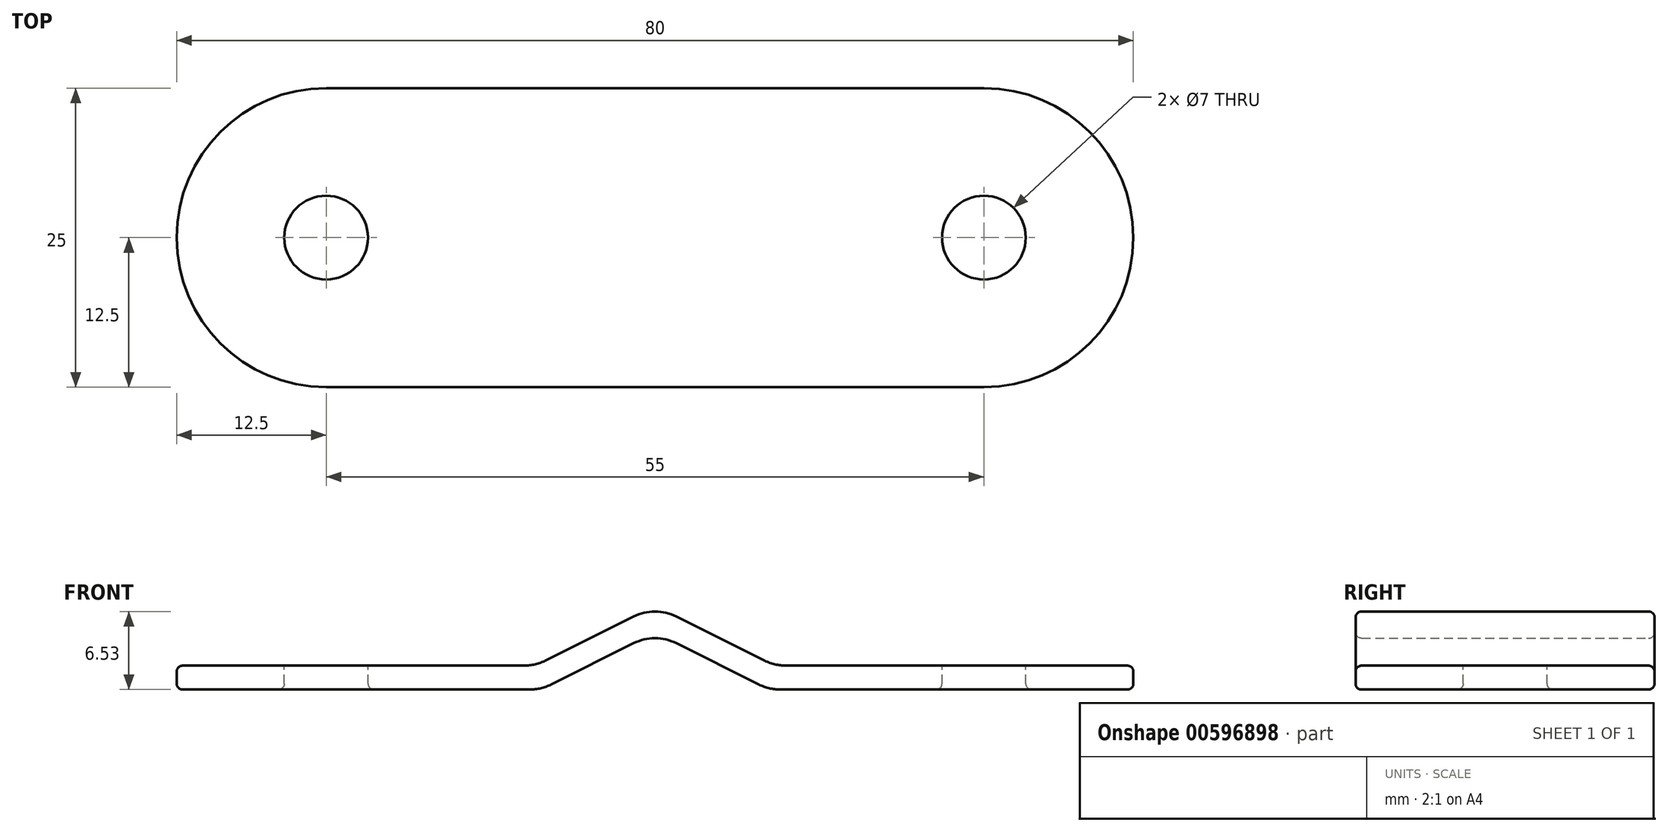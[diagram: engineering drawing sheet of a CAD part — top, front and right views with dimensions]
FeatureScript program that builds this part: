
annotation { "Feature Type Name" : "Feature", "Feature Type Description" : "" }
export const myFeature = defineFeature(function(context is Context, id is Id, definition is map)
    precondition{}
    {
        {
            var Q0;
            Q0=qCreatedBy(makeId("Front.planeOp"),FACE);
            var sketch = newSketch(context, id + "F0", { "sketchPlane" : qUnion([Q0])});
            skLineSegment(sketch, "E0", {"start": v(-40, 0) * mm, "end": v(-10, 0) * mm});
            skLineSegment(sketch, "E1", {"start": v(-10, 0) * mm, "end": v(0, 5) * mm});
            skLineSegment(sketch, "E2.MirrorCS", {"start": v(40, 0) * mm, "end": v(10, 0) * mm});
            skLineSegment(sketch, "E3.MirrorCS", {"start": v(10, 0) * mm, "end": v(0, 5) * mm});
            skLineSegment(sketch, "E4.0", {"start": v(40, -2) * mm, "end": v(9.53, -2) * mm});
            skLineSegment(sketch, "E4.1", {"start": v(9.53, -2) * mm, "end": v(0, 2.76) * mm});
            skLineSegment(sketch, "E4.2", {"start": v(-9.53, -2) * mm, "end": v(0, 2.76) * mm});
            skLineSegment(sketch, "E4.3", {"start": v(-40, -2) * mm, "end": v(-9.53, -2) * mm});
            skLineSegment(sketch, "E5", {"start": v(-40, 0) * mm, "end": v(-40, -2) * mm});
            skLineSegment(sketch, "E6", {"start": v(40, 0) * mm, "end": v(40, -2) * mm});
            skSolve(sketch);
        }
        {
            var Q0;
            Q0=makeQuery(id+"F0.imprint","IMPRINT",FACE,{"disambiguationData":[TD([[makeQuery(id+"F0.imprint","IMPRINT",EDGE,{"derivedFrom":sQuery(id+"F0.wireOp",EDGE,"E0")}),-1.0]])]});
            extrude(context, id + "F1", {"entities" : qUnion([Q0]), "depth" : 25 * mm, "offsetDistance" : 25 * mm, "symmetric" : true});
        }
        {
            var Q0;
            Q0=qCreatedBy(makeId("Top.planeOp"),FACE);
            var sketch = newSketch(context, id + "F2", { "sketchPlane" : qUnion([Q0])});
            skLineSegment(sketch, "E7", {"start": v(-27.5, 12.5) * mm, "end": v(-27.5, -12.5) * mm, "construction": true});
            skLineSegment(sketch, "E8", {"start": v(27.5, 12.5) * mm, "end": v(27.5, -12.5) * mm, "construction": true});
            skCircle(sketch, "E9", {"center": v(-27.5, 0) * mm, "radius": 12.5 * mm});
            skCircle(sketch, "E10", {"center": v(27.5, 0) * mm, "radius": 12.5 * mm});
            skCircle(sketch, "E11", {"center": v(-27.5, 0) * mm, "radius": 3.5 * mm});
            skCircle(sketch, "E12", {"center": v(27.5, 0) * mm, "radius": 3.5 * mm});
            skSolve(sketch);
        }
        {
            var Q0;
            Q0=makeQuery(id+"F2.imprint","IMPRINT",FACE,{"disambiguationData":[TD([[makeQuery(id+"F2.imprint","IMPRINT",EDGE,{"derivedFrom":sQuery(id+"F2.wireOp",EDGE,"E11")}),1.0]])]});
            var Q1;
            Q1=makeQuery(id+"F2.imprint","IMPRINT",FACE,{"disambiguationData":[TD([[makeQuery(id+"F2.imprint","IMPRINT",EDGE,{"derivedFrom":sQuery(id+"F2.wireOp",EDGE,"E12")}),1.0]])]});
            var Q2;
            Q2=sQuery(id+"F2.wireOp",EDGE,"E11");
            var Q3;
            Q3=sQuery(id+"F2.wireOp",EDGE,"E12");
            extrude(context, id + "F3", {"entities" : qUnion([Q0, Q1]), "operationType" : NewBodyOperationType.REMOVE, "surfaceEntities" : qUnion([Q2, Q3]), "endBound" : BoundingType.THROUGH_ALL, "oppositeDirection" : true, "depth" : 25 * mm, "offsetDistance" : 25 * mm});
        }
        {
            var Q0;
            Q0=makeQuery(id+"F1.opExtrude","SWEPT_FACE",FACE,{"disambiguationData":[OSD([sQuery(id+"F0.wireOp",EDGE,"E0")])]});
            var sketch = newSketch(context, id + "F4", { "sketchPlane" : qUnion([Q0])});
            skCircle(sketch, "E13.0", {"center": v(-27.5, 0) * mm, "radius": 12.5 * mm});
            skSolve(sketch);
        }
        {
            var Q0;
            Q0=makeQuery(id+"F1.opExtrude","SWEPT_FACE",FACE,{"disambiguationData":[OSD([sQuery(id+"F0.wireOp",EDGE,"E2.MirrorCS")])]});
            var sketch = newSketch(context, id + "F5", { "sketchPlane" : qUnion([Q0])});
            skCircle(sketch, "E14", {"center": v(27.5, 0) * mm, "radius": 12.5 * mm});
            skSolve(sketch);
        }
        {
            var Q0;
            {var subQ0=sQuery(id+"F4.wireOp",EDGE,"E13.0");var subQ1=sQuery(id+"F0.wireOp",EDGE,"E0");var subQ4=makeQuery(id+"F1.opExtrude","CAP_EDGE",EDGE,{"disambiguationData":[OSD([subQ1])],"isStart":false});var subQ5=makeQuery(id+"F4.imprint","INTERSECT",VERTEX,{"derivedFrom":[subQ4,subQ0]});Q0=makeQuery(id+"F4.imprint","IMPRINT",FACE,{"disambiguationData":[TD([[makeQuery(id+"F4.imprint","IMPRINT",EDGE,{"disambiguationData":[TD([[subQ5,1.0]])],"derivedFrom":subQ0}),-1.0]])]});}
            var Q1;
            {var subQ0=sQuery(id+"F4.wireOp",EDGE,"E13.0");var subQ1=sQuery(id+"F0.wireOp",EDGE,"E0");var subQ4=makeQuery(id+"F1.opExtrude","CAP_EDGE",EDGE,{"disambiguationData":[OSD([subQ1])],"isStart":true});var subQ5=makeQuery(id+"F4.imprint","INTERSECT",VERTEX,{"derivedFrom":[subQ4,subQ0]});Q1=makeQuery(id+"F4.imprint","IMPRINT",FACE,{"disambiguationData":[TD([[makeQuery(id+"F4.imprint","IMPRINT",EDGE,{"disambiguationData":[TD([[subQ5,-1.0]])],"derivedFrom":subQ0}),-1.0]])]});}
            var Q2;
            {var subQ0=sQuery(id+"F5.wireOp",EDGE,"E14");var subQ1=sQuery(id+"F0.wireOp",EDGE,"E2.MirrorCS");var subQ4=makeQuery(id+"F1.opExtrude","CAP_EDGE",EDGE,{"disambiguationData":[OSD([subQ1])],"isStart":false});var subQ5=makeQuery(id+"F5.imprint","INTERSECT",VERTEX,{"derivedFrom":[subQ4,subQ0]});Q2=makeQuery(id+"F5.imprint","IMPRINT",FACE,{"disambiguationData":[TD([[makeQuery(id+"F5.imprint","IMPRINT",EDGE,{"disambiguationData":[TD([[subQ5,-1.0]])],"derivedFrom":subQ0}),-1.0]])]});}
            var Q3;
            {var subQ0=sQuery(id+"F5.wireOp",EDGE,"E14");var subQ1=sQuery(id+"F0.wireOp",EDGE,"E2.MirrorCS");var subQ2=makeQuery(id+"F1.opExtrude","CAP_EDGE",EDGE,{"disambiguationData":[OSD([subQ1])],"isStart":true});var subQ3=makeQuery(id+"F5.imprint","INTERSECT",VERTEX,{"derivedFrom":[subQ2,subQ0]});Q3=makeQuery(id+"F5.imprint","IMPRINT",FACE,{"disambiguationData":[TD([[makeQuery(id+"F5.imprint","IMPRINT",EDGE,{"disambiguationData":[TD([[subQ3,1.0]])],"derivedFrom":subQ0}),-1.0]])]});}
            extrude(context, id + "F6", {"entities" : qUnion([Q0, Q1, Q2, Q3]), "operationType" : NewBodyOperationType.REMOVE, "endBound" : BoundingType.THROUGH_ALL, "oppositeDirection" : true, "depth" : 25 * mm, "offsetDistance" : 25 * mm});
        }
        {
            var Q0;
            Q0=makeQuery(id+"F1.opExtrude","SWEPT_EDGE",EDGE,{"disambiguationData":[OSD([sQuery(id+"F0.wireOp",EDGE,"E1"),sQuery(id+"F0.wireOp",EDGE,"E3.MirrorCS")])]});
            var Q1;
            Q1=makeQuery(id+"F1.opExtrude","SWEPT_EDGE",EDGE,{"disambiguationData":[OSD([sQuery(id+"F0.wireOp",EDGE,"E2.MirrorCS"),sQuery(id+"F0.wireOp",EDGE,"E3.MirrorCS")])]});
            var Q2;
            Q2=makeQuery(id+"F1.opExtrude","SWEPT_EDGE",EDGE,{"disambiguationData":[OSD([sQuery(id+"F0.wireOp",EDGE,"E0"),sQuery(id+"F0.wireOp",EDGE,"E1")])]});
            var Q3;
            Q3=makeQuery(id+"F1.opExtrude","SWEPT_EDGE",EDGE,{"disambiguationData":[OSD([sQuery(id+"F0.wireOp",EDGE,"E4.1"),sQuery(id+"F0.wireOp",EDGE,"E4.2")])]});
            var Q4;
            Q4=makeQuery(id+"F1.opExtrude","SWEPT_EDGE",EDGE,{"disambiguationData":[OSD([sQuery(id+"F0.wireOp",EDGE,"E4.0"),sQuery(id+"F0.wireOp",EDGE,"E4.1")])]});
            var Q5;
            Q5=makeQuery(id+"F1.opExtrude","SWEPT_EDGE",EDGE,{"disambiguationData":[OSD([sQuery(id+"F0.wireOp",EDGE,"E4.2"),sQuery(id+"F0.wireOp",EDGE,"E4.3")])]});
            fillet(context, id + "F7", {"entities" : qUnion([Q0, Q1, Q2, Q3, Q4, Q5]), "tangentPropagation" : true, "radius" : 4 * mm, "defaultsChanged" : false, "vertexSettings" : [], "allowEdgeOverflow" : false});
        }
        {
            var Q0;
            Q0=makeQuery(id+"F1.opExtrude","CAP_EDGE",EDGE,{"disambiguationData":[OSD([sQuery(id+"F0.wireOp",EDGE,"E2.MirrorCS")])],"isStart":true});
            var Q1;
            Q1=makeQuery(id+"F1.opExtrude","CAP_EDGE",EDGE,{"disambiguationData":[OSD([sQuery(id+"F0.wireOp",EDGE,"E4.0")])],"isStart":true});
            var Q2;
            Q2=makeQuery(id+"F3.boolean.opBoolean","INTERSECT",EDGE,{"derivedFrom":[makeQuery(id+"F1.opExtrude","SWEPT_FACE",FACE,{"disambiguationData":[OSD([sQuery(id+"F0.wireOp",EDGE,"E4.0")])]}),makeQuery(id+"F3.opExtrude","SWEPT_FACE",FACE,{"disambiguationData":[OSD([sQuery(id+"F2.wireOp",EDGE,"E12")])]})]});
            var Q3;
            Q3=makeQuery(id+"F3.boolean.opBoolean","INTERSECT",EDGE,{"derivedFrom":[makeQuery(id+"F1.opExtrude","SWEPT_FACE",FACE,{"disambiguationData":[OSD([sQuery(id+"F0.wireOp",EDGE,"E4.3")])]}),makeQuery(id+"F3.opExtrude","SWEPT_FACE",FACE,{"disambiguationData":[OSD([sQuery(id+"F2.wireOp",EDGE,"E11")])]})]});
            var Q4;
            Q4=makeQuery(id+"F3.boolean.opBoolean","COPY",EDGE,{"derivedFrom":makeQuery(id+"F3.opExtrude","CAP_EDGE",EDGE,{"disambiguationData":[OSD([sQuery(id+"F2.wireOp",EDGE,"E11")])],"isStart":true})});
            var Q5;
            Q5=makeQuery(id+"F3.boolean.opBoolean","COPY",EDGE,{"derivedFrom":makeQuery(id+"F3.opExtrude","CAP_EDGE",EDGE,{"disambiguationData":[OSD([sQuery(id+"F2.wireOp",EDGE,"E12")])],"isStart":true})});
            fillet(context, id + "F8", {"entities" : qUnion([Q0, Q1, Q2, Q3, Q4, Q5]), "tangentPropagation" : true, "radius" : 0.5 * mm, "defaultsChanged" : false, "vertexSettings" : [], "allowEdgeOverflow" : false});
        }
    });
